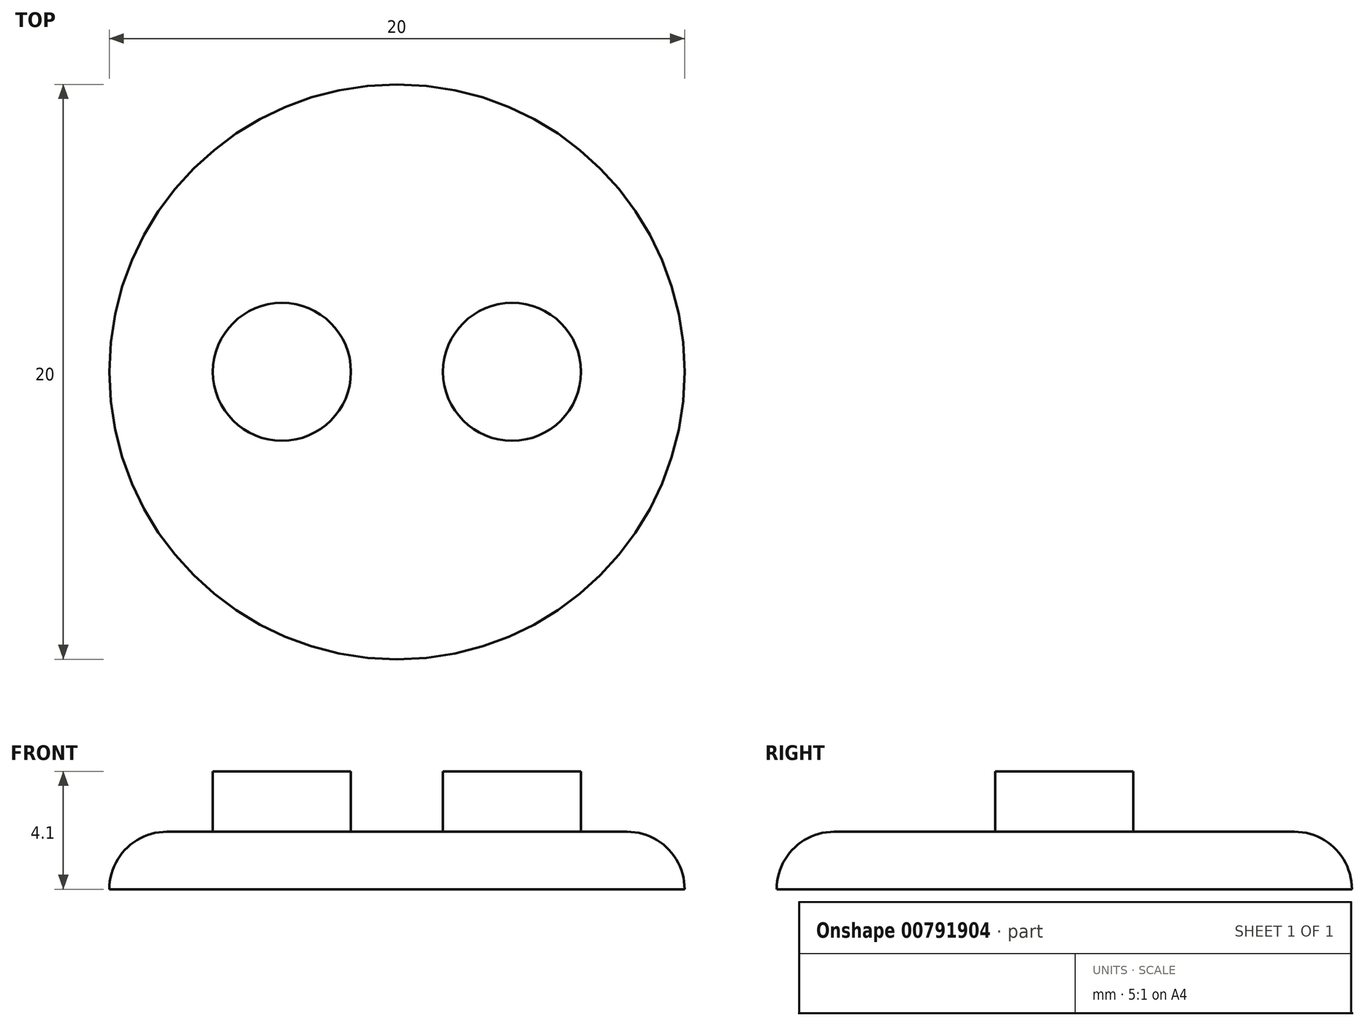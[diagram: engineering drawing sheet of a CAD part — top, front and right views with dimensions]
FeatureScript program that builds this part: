
annotation { "Feature Type Name" : "Feature", "Feature Type Description" : "" }
export const myFeature = defineFeature(function(context is Context, id is Id, definition is map)
    precondition{}
    {
        {
            var Q0;
            Q0=qCreatedBy(makeId("Top.planeOp"),FACE);
            var sketch = newSketch(context, id + "F0", { "sketchPlane" : qUnion([Q0])});
            skCircle(sketch, "E0", {"center": v(0, 0) * mm, "radius": 10 * mm});
            skSolve(sketch);
        }
        {
            var Q0;
            Q0=makeQuery(id+"F0.imprint","IMPRINT",FACE,{"disambiguationData":[TD([[makeQuery(id+"F0.imprint","IMPRINT",EDGE,{"derivedFrom":sQuery(id+"F0.wireOp",EDGE,"E0")}),1.0]])]});
            extrude(context, id + "F1", {"entities" : qUnion([Q0]), "depth" : 2 * mm, "offsetDistance" : 25 * mm});
        }
        {
            var Q0;
            Q0=makeQuery(id+"F1.opExtrude","CAP_EDGE",EDGE,{"disambiguationData":[OSD([sQuery(id+"F0.wireOp",EDGE,"E0")])],"isStart":false});
            fillet(context, id + "F2", {"entities" : qUnion([Q0]), "radius" : 2 * mm, "tangentPropagation" : true, "allowEdgeOverflow" : false});
        }
        {
            var Q0;
            Q0=makeQuery(id+"F1.opExtrude","CAP_FACE",FACE,{"disambiguationData":[OSD([sQuery(id+"F0.wireOp",EDGE,"E0")])],"isStart":false});
            var sketch = newSketch(context, id + "F3", { "sketchPlane" : qUnion([Q0])});
            skCircle(sketch, "E1", {"center": v(-4, 0) * mm, "radius": 2.4 * mm});
            skCircle(sketch, "E2", {"center": v(4, 0) * mm, "radius": 2.4 * mm});
            skSolve(sketch);
        }
        {
            var Q0;
            Q0 = qSketchRegion(id + "F3", true);
            extrude(context, id + "F4", {"entities" : qUnion([Q0]), "operationType" : NewBodyOperationType.ADD, "depth" : 2.1 * mm, "offsetDistance" : 25 * mm});
        }
    });
